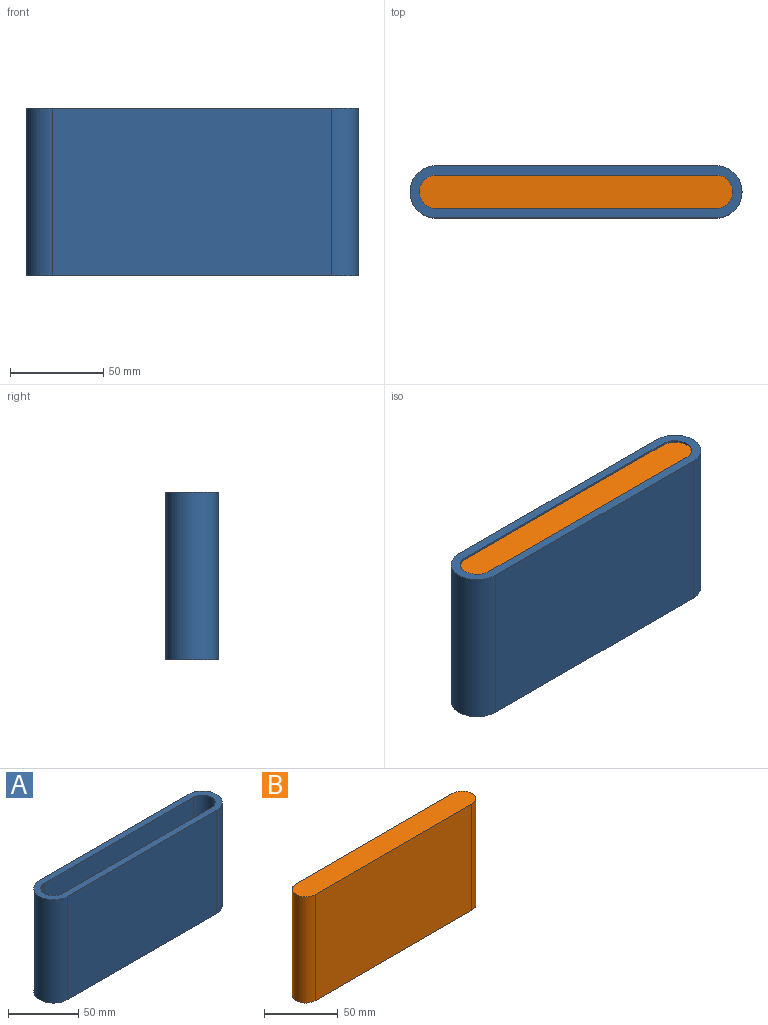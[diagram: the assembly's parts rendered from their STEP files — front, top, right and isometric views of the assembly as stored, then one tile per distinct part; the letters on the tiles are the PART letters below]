
ASSEMBLY  parts=2 mates=1
PART A: 10 faces, bbox 178x28x90 mm
  f0: plane 150x90mm, normal (0,1,0), area 13500mm2, adj f1,f7,f8,f9
  f1: cylinder r=9mm len=90mm, axis (0,0,-1), area 2544.7mm2, adj f0,f2,f8,f9
  f2: plane 150x90mm, normal (0,-1,0), area 13500mm2, adj f1,f7,f8,f9
  f3: plane 150x90mm, normal (0,1,0), area 13500mm2, adj f4,f6,f8,f9
  f4: cylinder r=14mm len=90mm, axis (0,0,-1), area 3958.4mm2, adj f3,f5,f8,f9
  f5: plane 150x90mm, normal (0,-1,0), area 13500mm2, adj f4,f6,f8,f9
  f6: cylinder r=14mm len=90mm, axis (0,0,-1), area 3958.4mm2, adj f3,f5,f8,f9
  f7: cylinder r=9mm len=90mm, axis (0,0,-1), area 2544.7mm2, adj f0,f2,f8,f9
  f8: plane 178x28mm, normal (0,0,1), area 1861.3mm2, adj f0,f1,f2,f3,f4,f5,f6,f7
  f9: plane 178x28mm, normal (0,0,-1), area 1861.3mm2, adj f0,f1,f2,f3,f4,f5,f6,f7
PART B: 6 faces, bbox 168x18x88 mm
  f0: plane 150x88mm, normal (0,1,0), area 13200.1mm2, adj f1,f3,f4,f5
  f1: cylinder r=9mm len=88mm, axis (0,0,-1), area 2488.1mm2, adj f0,f2,f4,f5
  f2: plane 150x88mm, normal (0,-1,0), area 13200.1mm2, adj f1,f3,f4,f5
  f3: cylinder r=9mm len=88mm, axis (0,0,-1), area 2488.1mm2, adj f0,f2,f4,f5
  f4: plane 168x18mm, normal (0,0,1), area 2954.5mm2, adj f0,f1,f2,f3
  f5: plane 168x18mm, normal (0,0,-1), area 2954.5mm2, adj f0,f1,f2,f3
PLACE A t=(-12.98,33.93,-26.82)mm
PLACE B t=(-12.98,-15.03,-25.82)mm
MATE fastened B.f3 <-> A.f6  axis (0,0,1) through (137.02,47.93,62.18)mm
